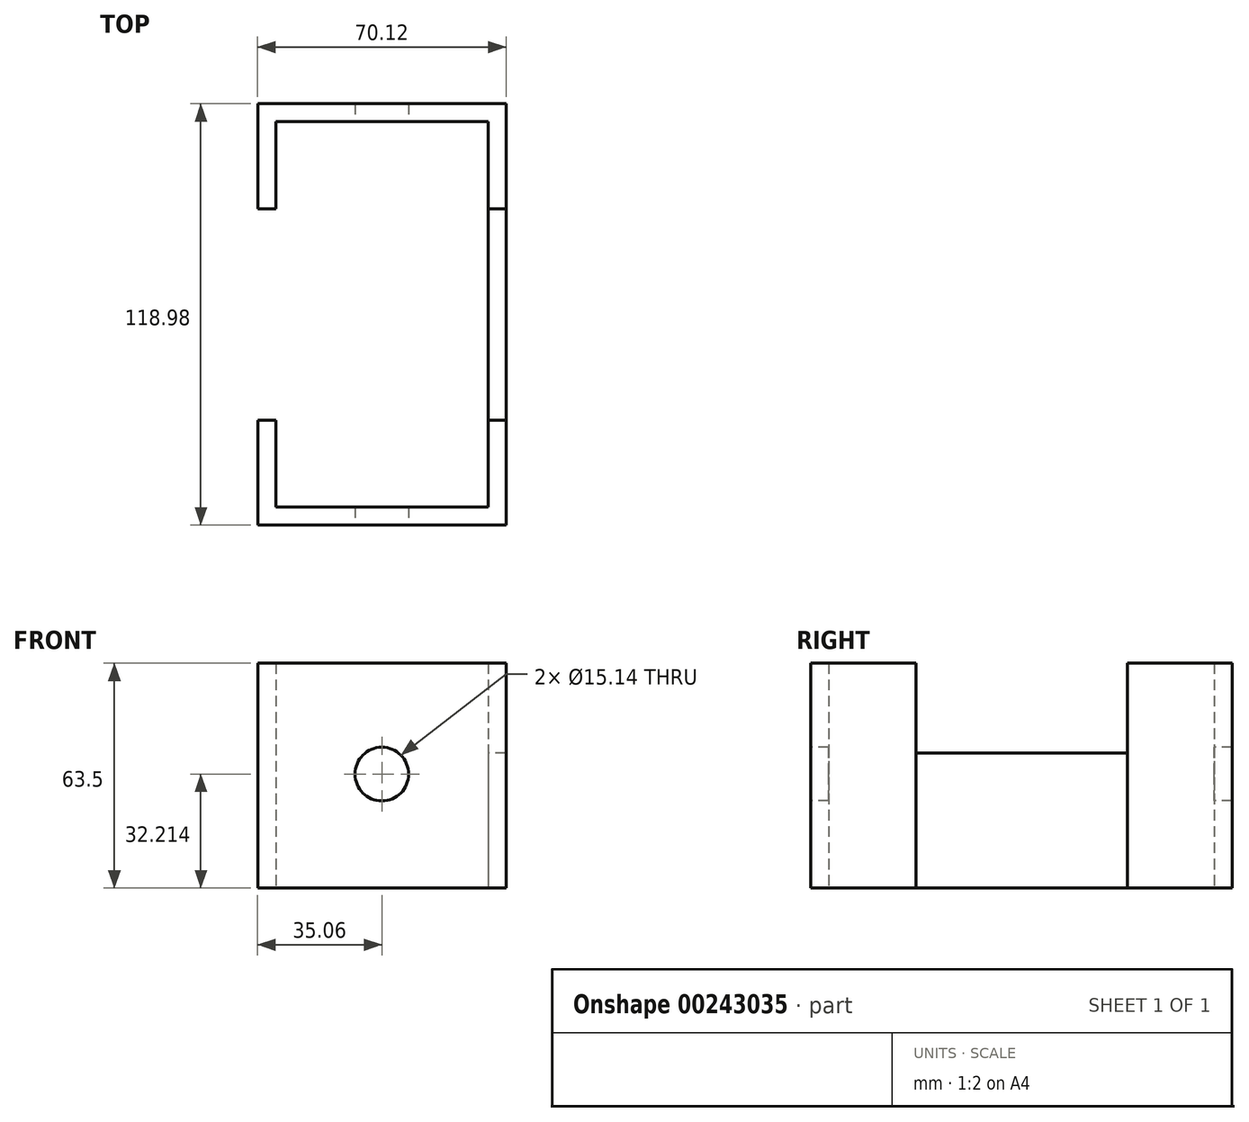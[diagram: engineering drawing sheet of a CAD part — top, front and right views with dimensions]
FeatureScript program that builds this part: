
annotation { "Feature Type Name" : "Feature", "Feature Type Description" : "" }
export const myFeature = defineFeature(function(context is Context, id is Id, definition is map)
    precondition{}
    {
        {
            var Q0;
            Q0=qCreatedBy(makeId("Top.planeOp"),FACE);
            var sketch = newSketch(context, id + "F0", { "sketchPlane" : qUnion([Q0])});
            skLineSegment(sketch, "E0.bottom", {"start": v(35.06, -59.5) * mm, "end": v(-35.06, -59.5) * mm});
            skLineSegment(sketch, "E0.top", {"start": v(35.06, 59.5) * mm, "end": v(-35.06, 59.5) * mm});
            skLineSegment(sketch, "E0.left", {"start": v(35.06, -59.5) * mm, "end": v(35.06, 59.5) * mm});
            skLineSegment(sketch, "E0.right", {"start": v(-35.06, -59.5) * mm, "end": v(-35.06, 59.5) * mm});
            skPoint(sketch, "E0.middle", {"position": v(0, 0) * mm});
            skLineSegment(sketch, "E1.bottom", {"start": v(29.98, -54.41) * mm, "end": v(-29.98, -54.41) * mm});
            skLineSegment(sketch, "E1.top", {"start": v(29.98, 54.41) * mm, "end": v(-29.98, 54.41) * mm});
            skLineSegment(sketch, "E1.left", {"start": v(29.98, -54.41) * mm, "end": v(29.98, 54.41) * mm});
            skLineSegment(sketch, "E1.right", {"start": v(-29.98, -54.41) * mm, "end": v(-29.98, 54.41) * mm});
            skLineSegment(sketch, "E2.bottom", {"start": v(35.06, 29.82) * mm, "end": v(29.98, 29.82) * mm});
            skLineSegment(sketch, "E2.top", {"start": v(35.06, -29.82) * mm, "end": v(29.98, -29.82) * mm});
            skLineSegment(sketch, "E2.left", {"start": v(35.06, 29.82) * mm, "end": v(35.06, -29.82) * mm});
            skLineSegment(sketch, "E2.right", {"start": v(-35.06, 29.82) * mm, "end": v(-35.06, -29.82) * mm});
            skLineSegment(sketch, "E3.trimOffspring", {"start": v(-29.98, 29.82) * mm, "end": v(-35.06, 29.82) * mm});
            skLineSegment(sketch, "E4.trimOffspring", {"start": v(-29.98, -29.82) * mm, "end": v(-35.06, -29.82) * mm});
            skSolve(sketch);
        }
        {
            var Q0;
            {var subQ4=sQuery(id+"F0.wireOp",EDGE,"E0.top");Q0=makeQuery(id+"F0.imprint","IMPRINT",FACE,{"disambiguationData":[TD([[makeQuery(id+"F0.imprint","IMPRINT",EDGE,{"derivedFrom":subQ4}),1.0]])]});}
            var Q1;
            {var subQ2=sQuery(id+"F0.wireOp",EDGE,"E0.bottom");Q1=makeQuery(id+"F0.imprint","IMPRINT",FACE,{"disambiguationData":[TD([[makeQuery(id+"F0.imprint","IMPRINT",EDGE,{"derivedFrom":subQ2}),-1.0]])]});}
            extrude(context, id + "F1", {"entities" : qUnion([Q0, Q1]), "depth" : 63.5 * mm});
        }
        {
            var Q0;
            Q0=makeQuery(id+"F0.imprint","IMPRINT",FACE,{"disambiguationData":[TD([[makeQuery(id+"F0.imprint","IMPRINT",EDGE,{"derivedFrom":sQuery(id+"F0.wireOp",EDGE,"E2.right")}),1.0]])]});
            var Q1;
            {var subQ0=sQuery(id+"F0.wireOp",EDGE,"E2.bottom");Q1=makeQuery(id+"F0.imprint","IMPRINT",FACE,{"disambiguationData":[TD([[makeQuery(id+"F0.imprint","IMPRINT",EDGE,{"derivedFrom":subQ0}),1.0]])]});}
            extrude(context, id + "F2", {"entities" : qUnion([Q0, Q1]), "depth" : 38.1 * mm});
        }
        {
            var Q0;
            Q0=makeQuery(id+"F1.opExtrude","SWEPT_FACE",FACE,{"disambiguationData":[OSD([sQuery(id+"F0.wireOp",EDGE,"E0.bottom")])]});
            var sketch = newSketch(context, id + "F3", { "sketchPlane" : qUnion([Q0])});
            skCircle(sketch, "E5", {"center": v(0, 32.21) * mm, "radius": 7.57 * mm});
            skPoint(sketch, "E5.centerSnap0", {"position": v(0, 0) * mm});
            skSolve(sketch);
        }
        {
            var Q0;
            Q0=makeQuery(id+"F3.imprint","IMPRINT",FACE,{"disambiguationData":[TD([[makeQuery(id+"F3.imprint","IMPRINT",EDGE,{"derivedFrom":sQuery(id+"F3.wireOp",EDGE,"E5")}),1.0]])]});
            extrude(context, id + "F4", {"entities" : qUnion([Q0]), "operationType" : NewBodyOperationType.REMOVE, "oppositeDirection" : true, "depth" : 124.2 * mm});
        }
    });
